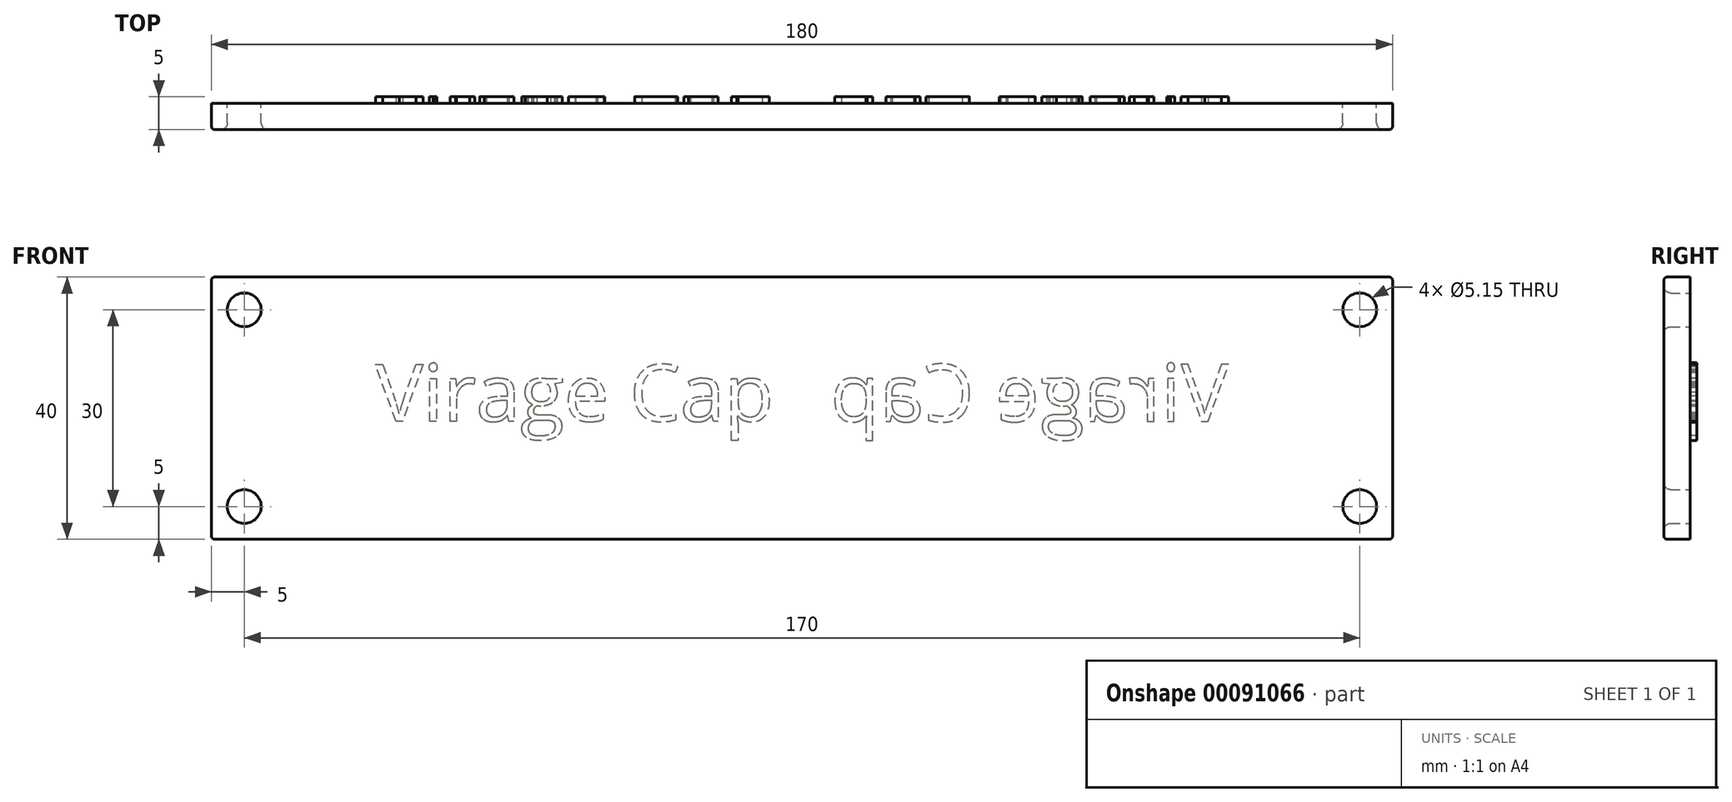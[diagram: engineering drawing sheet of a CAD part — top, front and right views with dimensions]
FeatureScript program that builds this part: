
annotation { "Feature Type Name" : "Feature", "Feature Type Description" : "" }
export const myFeature = defineFeature(function(context is Context, id is Id, definition is map)
    precondition{}
    {
        {
            var Q0;
            Q0=qCreatedBy(makeId("Front.planeOp"),FACE);
            var sketch = newSketch(context, id + "F0", { "sketchPlane" : qUnion([Q0])});
            skLineSegment(sketch, "E0.bottom", {"start": v(-90, -20) * mm, "end": v(90, -20) * mm});
            skLineSegment(sketch, "E0.top", {"start": v(-90, 20) * mm, "end": v(90, 20) * mm});
            skLineSegment(sketch, "E0.left", {"start": v(-90, -20) * mm, "end": v(-90, 20) * mm});
            skLineSegment(sketch, "E0.right", {"start": v(90, -20) * mm, "end": v(90, 20) * mm});
            skPoint(sketch, "E0.middle", {"position": v(0, 0) * mm});
            skCircle(sketch, "E1", {"center": v(-85, 15) * mm, "radius": 2.58 * mm});
            skPoint(sketch, "E2.start.orphan", {"position": v(-90, 0) * mm});
            skPoint(sketch, "E3.orphan", {"position": v(0, 20) * mm});
            skPoint(sketch, "E4.end.orphan", {"position": v(0, -20) * mm});
            skLineSegment(sketch, "E5", {"start": v(-90, 0) * mm, "end": v(0, 0) * mm, "construction": true});
            skLineSegment(sketch, "E6", {"start": v(0, 20) * mm, "end": v(0, -20) * mm, "construction": true});
            skCircle(sketch, "E7.MirrorC", {"center": v(-85, -15) * mm, "radius": 2.58 * mm});
            skCircle(sketch, "E8.MirrorC", {"center": v(85, 15) * mm, "radius": 2.58 * mm});
            skCircle(sketch, "E9.MirrorC", {"center": v(85, -15) * mm, "radius": 2.58 * mm});
            skSolve(sketch);
        }
        {
            var Q0;
            Q0=makeQuery(id+"F0.imprint","IMPRINT",FACE,{"disambiguationData":[TD([[makeQuery(id+"F0.imprint","IMPRINT",EDGE,{"derivedFrom":sQuery(id+"F0.wireOp",EDGE,"E0.bottom")}),1.0]])]});
            extrude(context, id + "F1", {"entities" : qUnion([Q0]), "depth" : 4 * mm});
        }
        {
            var Q0;
            Q0=makeQuery(id+"F1.opExtrude","CAP_EDGE",EDGE,{"disambiguationData":[OSD([sQuery(id+"F0.wireOp",EDGE,"E1")])],"isStart":false});
            var Q1;
            Q1=makeQuery(id+"F1.opExtrude","CAP_EDGE",EDGE,{"disambiguationData":[OSD([sQuery(id+"F0.wireOp",EDGE,"f5b72a5b-8583-449a-bdbf-9ac5a681e1fd0.MirrorC")])],"isStart":false});
            var Q2;
            Q2=makeQuery(id+"F1.opExtrude","CAP_EDGE",EDGE,{"disambiguationData":[OSD([sQuery(id+"F0.wireOp",EDGE,"2623e306-60f4-4522-aa65-1e3e8c2cf5b60.MirrorC")])],"isStart":false});
            var Q3;
            Q3=makeQuery(id+"F1.opExtrude","CAP_EDGE",EDGE,{"disambiguationData":[OSD([sQuery(id+"F0.wireOp",EDGE,"be81a34d-1d50-4ce7-a7a8-4484a1701fac0.MirrorC")])],"isStart":false});
            var Q4;
            Q4=makeQuery(id+"F1.opExtrude","CAP_EDGE",EDGE,{"disambiguationData":[OSD([sQuery(id+"F0.wireOp",EDGE,"E7.MirrorC")])],"isStart":false});
            var Q5;
            Q5=makeQuery(id+"F1.opExtrude","CAP_EDGE",EDGE,{"disambiguationData":[OSD([sQuery(id+"F0.wireOp",EDGE,"E8.MirrorC")])],"isStart":false});
            var Q6;
            Q6=makeQuery(id+"F1.opExtrude","CAP_EDGE",EDGE,{"disambiguationData":[OSD([sQuery(id+"F0.wireOp",EDGE,"E9.MirrorC")])],"isStart":false});
            fillet(context, id + "F2", {"entities" : qUnion([Q0, Q1, Q2, Q3, Q4, Q5, Q6]), "radius" : 1 * mm, "tangentPropagation" : true, "allowEdgeOverflow" : false});
        }
        {
            var Q0;
            Q0=makeQuery(id+"F1.opExtrude","CAP_EDGE",EDGE,{"disambiguationData":[OSD([sQuery(id+"F0.wireOp",EDGE,"E0.top")])],"isStart":false});
            var Q1;
            Q1=makeQuery(id+"F1.opExtrude","CAP_EDGE",EDGE,{"disambiguationData":[OSD([sQuery(id+"F0.wireOp",EDGE,"E0.left")])],"isStart":false});
            var Q2;
            Q2=makeQuery(id+"F1.opExtrude","CAP_EDGE",EDGE,{"disambiguationData":[OSD([sQuery(id+"F0.wireOp",EDGE,"E0.bottom")])],"isStart":false});
            var Q3;
            Q3=makeQuery(id+"F1.opExtrude","CAP_EDGE",EDGE,{"disambiguationData":[OSD([sQuery(id+"F0.wireOp",EDGE,"E0.right")])],"isStart":false});
            var Q4;
            Q4=makeQuery(id+"F1.opExtrude","SWEPT_EDGE",EDGE,{"disambiguationData":[OSD([sQuery(id+"F0.wireOp",EDGE,"E0.top"),sQuery(id+"F0.wireOp",EDGE,"E0.left")])]});
            var Q5;
            Q5=makeQuery(id+"F1.opExtrude","SWEPT_EDGE",EDGE,{"disambiguationData":[OSD([sQuery(id+"F0.wireOp",EDGE,"E0.bottom"),sQuery(id+"F0.wireOp",EDGE,"E0.left")])]});
            var Q6;
            Q6=makeQuery(id+"F1.opExtrude","SWEPT_EDGE",EDGE,{"disambiguationData":[OSD([sQuery(id+"F0.wireOp",EDGE,"E0.top"),sQuery(id+"F0.wireOp",EDGE,"E0.right")])]});
            var Q7;
            Q7=makeQuery(id+"F1.opExtrude","SWEPT_EDGE",EDGE,{"disambiguationData":[OSD([sQuery(id+"F0.wireOp",EDGE,"E0.bottom"),sQuery(id+"F0.wireOp",EDGE,"E0.right")])]});
            fillet(context, id + "F3", {"entities" : qUnion([Q0, Q1, Q2, Q3, Q4, Q5, Q6, Q7]), "radius" : .5 * mm, "tangentPropagation" : true, "allowEdgeOverflow" : false});
        }
        {
            var Q0;
            Q0=makeQuery(id+"F1.opExtrude","CAP_FACE",FACE,{"disambiguationData":[OSD([sQuery(id+"F0.wireOp",EDGE,"E0.bottom"),sQuery(id+"F0.wireOp",EDGE,"E0.top"),sQuery(id+"F0.wireOp",EDGE,"E0.left"),sQuery(id+"F0.wireOp",EDGE,"E0.right"),sQuery(id+"F0.wireOp",EDGE,"E1"),sQuery(id+"F0.wireOp",EDGE,"E7.MirrorC"),sQuery(id+"F0.wireOp",EDGE,"E8.MirrorC"),sQuery(id+"F0.wireOp",EDGE,"E9.MirrorC")])],"isStart":true});
            var sketch = newSketch(context, id + "F4", { "sketchPlane" : qUnion([Q0])});
            skText(sketch, "E10", { "text": "Virage Cap", "fontName": "OpenSans-Regular.ttf"});
            skLineSegment(sketch, "E11", {"start": v(0, 20) * mm, "end": v(0, -20) * mm, "construction": true});
            const initialGuessF4  = {"E10": [-0.065, -0.00202, 1, 0, 0.00877]};
            skSetInitialGuess(sketch, initialGuessF4);
            skSolve(sketch);
        }
        {
            var Q0;
            Q0 = qSketchRegion(id + "F4", true);
            extrude(context, id + "F5", {"entities" : qUnion([Q0]), "operationType" : NewBodyOperationType.ADD, "depth" : 1 * mm});
        }
        {
            var Q0;
            Q0=makeQuery(id+"F1.opExtrude","SWEPT_BODY",BODY,{"disambiguationData":[OSD([sQuery(id+"F0.wireOp",EDGE,"E0.bottom"),sQuery(id+"F0.wireOp",EDGE,"E0.top"),sQuery(id+"F0.wireOp",EDGE,"E0.left"),sQuery(id+"F0.wireOp",EDGE,"E0.right"),sQuery(id+"F0.wireOp",EDGE,"E1"),sQuery(id+"F0.wireOp",EDGE,"E7.MirrorC"),sQuery(id+"F0.wireOp",EDGE,"E8.MirrorC"),sQuery(id+"F0.wireOp",EDGE,"E9.MirrorC")])]});
            var Q1;
            Q1=makeQuery(id+"F5.opExtrude","SWEPT_FACE",FACE,{"disambiguationData":[OSD([sQuery(id+"F4.wireOp",EDGE,"E10.sketch_text.stroke-94")])]});
            var Q2;
            Q2=makeQuery(id+"F5.opExtrude","SWEPT_FACE",FACE,{"disambiguationData":[OSD([sQuery(id+"F4.wireOp",EDGE,"E10.sketch_text.stroke-169")])]});
            var Q3;
            Q3=makeQuery(id+"F5.opExtrude","SWEPT_FACE",FACE,{"disambiguationData":[OSD([sQuery(id+"F4.wireOp",EDGE,"E10.sketch_text.stroke-185")])]});
            var Q4;
            Q4=makeQuery(id+"F5.opExtrude","SWEPT_FACE",FACE,{"disambiguationData":[OSD([sQuery(id+"F4.wireOp",EDGE,"E10.sketch_text.stroke-125")])]});
            var Q5;
            Q5=makeQuery(id+"F5.opExtrude","SWEPT_FACE",FACE,{"disambiguationData":[OSD([sQuery(id+"F4.wireOp",EDGE,"E10.sketch_text.stroke-155")])]});
            var Q6;
            Q6=makeQuery(id+"F5.opExtrude","SWEPT_FACE",FACE,{"disambiguationData":[OSD([sQuery(id+"F4.wireOp",EDGE,"E10.sketch_text.stroke-65")])]});
            var Q7;
            Q7=makeQuery(id+"F5.opExtrude","SWEPT_FACE",FACE,{"disambiguationData":[OSD([sQuery(id+"F4.wireOp",EDGE,"E10.sketch_text.stroke-81")])]});
            var Q8;
            Q8=makeQuery(id+"F5.opExtrude","SWEPT_FACE",FACE,{"disambiguationData":[OSD([sQuery(id+"F4.wireOp",EDGE,"E10.sketch_text.stroke-67")])]});
            var Q9;
            Q9=makeQuery(id+"F5.opExtrude","SWEPT_FACE",FACE,{"disambiguationData":[OSD([sQuery(id+"F4.wireOp",EDGE,"E10.sketch_text.stroke-99")])]});
            var Q10;
            Q10=makeQuery(id+"F5.opExtrude","SWEPT_FACE",FACE,{"disambiguationData":[OSD([sQuery(id+"F4.wireOp",EDGE,"E10.sketch_text.stroke-127")])]});
            var Q11;
            Q11=makeQuery(id+"F5.opExtrude","SWEPT_FACE",FACE,{"disambiguationData":[OSD([sQuery(id+"F4.wireOp",EDGE,"E10.sketch_text.stroke-10")])]});
            var Q12;
            Q12=makeQuery(id+"F5.opExtrude","CAP_FACE",FACE,{"disambiguationData":[OSD([sQuery(id+"F4.wireOp",EDGE,"E10.sketch_text.stroke-9"),sQuery(id+"F4.wireOp",EDGE,"E10.sketch_text.stroke-10"),sQuery(id+"F4.wireOp",EDGE,"E10.sketch_text.stroke-11"),sQuery(id+"F4.wireOp",EDGE,"E10.sketch_text.stroke-12")])],"isStart":false});
            var Q13;
            Q13=makeQuery(id+"F5.opExtrude","SWEPT_FACE",FACE,{"disambiguationData":[OSD([sQuery(id+"F4.wireOp",EDGE,"E10.sketch_text.stroke-154")])]});
            var Q14;
            Q14=makeQuery(id+"F5.opExtrude","SWEPT_FACE",FACE,{"disambiguationData":[OSD([sQuery(id+"F4.wireOp",EDGE,"E10.sketch_text.stroke-1")])]});
            var Q15;
            Q15=makeQuery(id+"F5.opExtrude","CAP_FACE",FACE,{"disambiguationData":[OSD([sQuery(id+"F4.wireOp",EDGE,"E10.sketch_text.stroke-124"),sQuery(id+"F4.wireOp",EDGE,"E10.sketch_text.stroke-125"),sQuery(id+"F4.wireOp",EDGE,"E10.sketch_text.stroke-126"),sQuery(id+"F4.wireOp",EDGE,"E10.sketch_text.stroke-127"),sQuery(id+"F4.wireOp",EDGE,"E10.sketch_text.stroke-128"),sQuery(id+"F4.wireOp",EDGE,"E10.sketch_text.stroke-129"),sQuery(id+"F4.wireOp",EDGE,"E10.sketch_text.stroke-130"),sQuery(id+"F4.wireOp",EDGE,"E10.sketch_text.stroke-131"),sQuery(id+"F4.wireOp",EDGE,"E10.sketch_text.stroke-132"),sQuery(id+"F4.wireOp",EDGE,"E10.sketch_text.stroke-133"),sQuery(id+"F4.wireOp",EDGE,"E10.sketch_text.stroke-134"),sQuery(id+"F4.wireOp",EDGE,"E10.sketch_text.stroke-135"),sQuery(id+"F4.wireOp",EDGE,"E10.sketch_text.stroke-136"),sQuery(id+"F4.wireOp",EDGE,"E10.sketch_text.stroke-137"),sQuery(id+"F4.wireOp",EDGE,"E10.sketch_text.stroke-138")])],"isStart":false});
            var Q16;
            Q16=makeQuery(id+"F5.opExtrude","CAP_FACE",FACE,{"disambiguationData":[OSD([sQuery(id+"F4.wireOp",EDGE,"E10.sketch_text.stroke-34"),sQuery(id+"F4.wireOp",EDGE,"E10.sketch_text.stroke-35"),sQuery(id+"F4.wireOp",EDGE,"E10.sketch_text.stroke-36"),sQuery(id+"F4.wireOp",EDGE,"E10.sketch_text.stroke-37"),sQuery(id+"F4.wireOp",EDGE,"E10.sketch_text.stroke-38"),sQuery(id+"F4.wireOp",EDGE,"E10.sketch_text.stroke-39"),sQuery(id+"F4.wireOp",EDGE,"E10.sketch_text.stroke-40"),sQuery(id+"F4.wireOp",EDGE,"E10.sketch_text.stroke-41"),sQuery(id+"F4.wireOp",EDGE,"E10.sketch_text.stroke-42"),sQuery(id+"F4.wireOp",EDGE,"E10.sketch_text.stroke-43"),sQuery(id+"F4.wireOp",EDGE,"E10.sketch_text.stroke-44"),sQuery(id+"F4.wireOp",EDGE,"E10.sketch_text.stroke-45"),sQuery(id+"F4.wireOp",EDGE,"E10.sketch_text.stroke-46"),sQuery(id+"F4.wireOp",EDGE,"E10.sketch_text.stroke-47"),sQuery(id+"F4.wireOp",EDGE,"E10.sketch_text.stroke-48"),sQuery(id+"F4.wireOp",EDGE,"E10.sketch_text.stroke-49"),sQuery(id+"F4.wireOp",EDGE,"E10.sketch_text.stroke-50"),sQuery(id+"F4.wireOp",EDGE,"E10.sketch_text.stroke-51"),sQuery(id+"F4.wireOp",EDGE,"E10.sketch_text.stroke-52"),sQuery(id+"F4.wireOp",EDGE,"E10.sketch_text.stroke-53"),sQuery(id+"F4.wireOp",EDGE,"E10.sketch_text.stroke-54"),sQuery(id+"F4.wireOp",EDGE,"E10.sketch_text.stroke-55"),sQuery(id+"F4.wireOp",EDGE,"E10.sketch_text.stroke-56"),sQuery(id+"F4.wireOp",EDGE,"E10.sketch_text.stroke-57"),sQuery(id+"F4.wireOp",EDGE,"E10.sketch_text.stroke-58"),sQuery(id+"F4.wireOp",EDGE,"E10.sketch_text.stroke-59"),sQuery(id+"F4.wireOp",EDGE,"E10.sketch_text.stroke-60")])],"isStart":false});
            var Q17;
            Q17=makeQuery(id+"F5.opExtrude","SWEPT_FACE",FACE,{"disambiguationData":[OSD([sQuery(id+"F4.wireOp",EDGE,"E10.sketch_text.stroke-50")])]});
            var Q18;
            Q18=makeQuery(id+"F5.opExtrude","SWEPT_FACE",FACE,{"disambiguationData":[OSD([sQuery(id+"F4.wireOp",EDGE,"E10.sketch_text.stroke-2")])]});
            var Q19;
            Q19=makeQuery(id+"F5.opExtrude","SWEPT_FACE",FACE,{"disambiguationData":[OSD([sQuery(id+"F4.wireOp",EDGE,"E10.sketch_text.stroke-3")])]});
            var Q20;
            Q20=makeQuery(id+"F5.opExtrude","SWEPT_FACE",FACE,{"disambiguationData":[OSD([sQuery(id+"F4.wireOp",EDGE,"E10.sketch_text.stroke-5")])]});
            var Q21;
            Q21=makeQuery(id+"F5.opExtrude","SWEPT_FACE",FACE,{"disambiguationData":[OSD([sQuery(id+"F4.wireOp",EDGE,"E10.sketch_text.stroke-8")])]});
            var Q22;
            Q22=makeQuery(id+"F5.opExtrude","SWEPT_FACE",FACE,{"disambiguationData":[OSD([sQuery(id+"F4.wireOp",EDGE,"E10.sketch_text.stroke-98")])]});
            var Q23;
            Q23=makeQuery(id+"F5.opExtrude","SWEPT_FACE",FACE,{"disambiguationData":[OSD([sQuery(id+"F4.wireOp",EDGE,"E10.sketch_text.stroke-66")])]});
            var Q24;
            Q24=makeQuery(id+"F5.opExtrude","SWEPT_FACE",FACE,{"disambiguationData":[OSD([sQuery(id+"F4.wireOp",EDGE,"E10.sketch_text.stroke-153")])]});
            var Q25;
            Q25=makeQuery(id+"F5.opExtrude","SWEPT_FACE",FACE,{"disambiguationData":[OSD([sQuery(id+"F4.wireOp",EDGE,"E10.sketch_text.stroke-126")])]});
            var Q26;
            Q26=makeQuery(id+"F5.opExtrude","SWEPT_FACE",FACE,{"disambiguationData":[OSD([sQuery(id+"F4.wireOp",EDGE,"E10.sketch_text.stroke-183")])]});
            var Q27;
            Q27=makeQuery(id+"F5.opExtrude","SWEPT_FACE",FACE,{"disambiguationData":[OSD([sQuery(id+"F4.wireOp",EDGE,"E10.sketch_text.stroke-109")])]});
            var Q28;
            Q28=makeQuery(id+"F5.opExtrude","SWEPT_FACE",FACE,{"disambiguationData":[OSD([sQuery(id+"F4.wireOp",EDGE,"E10.sketch_text.stroke-186")])]});
            var Q29;
            Q29=makeQuery(id+"F5.opExtrude","SWEPT_FACE",FACE,{"disambiguationData":[OSD([sQuery(id+"F4.wireOp",EDGE,"E10.sketch_text.stroke-79")])]});
            var Q30;
            Q30=makeQuery(id+"F5.opExtrude","SWEPT_FACE",FACE,{"disambiguationData":[OSD([sQuery(id+"F4.wireOp",EDGE,"E10.sketch_text.stroke-110")])]});
            var Q31;
            Q31=makeQuery(id+"F5.opExtrude","SWEPT_FACE",FACE,{"disambiguationData":[OSD([sQuery(id+"F4.wireOp",EDGE,"E10.sketch_text.stroke-38")])]});
            var Q32;
            Q32=makeQuery(id+"F5.opExtrude","SWEPT_FACE",FACE,{"disambiguationData":[OSD([sQuery(id+"F4.wireOp",EDGE,"E10.sketch_text.stroke-24")])]});
            var Q33;
            Q33=makeQuery(id+"F5.opExtrude","SWEPT_FACE",FACE,{"disambiguationData":[OSD([sQuery(id+"F4.wireOp",EDGE,"E10.sketch_text.stroke-12")])]});
            var Q34;
            Q34=makeQuery(id+"F5.opExtrude","SWEPT_FACE",FACE,{"disambiguationData":[OSD([sQuery(id+"F4.wireOp",EDGE,"E10.sketch_text.stroke-100")])]});
            var Q35;
            Q35=makeQuery(id+"F5.opExtrude","SWEPT_FACE",FACE,{"disambiguationData":[OSD([sQuery(id+"F4.wireOp",EDGE,"E10.sketch_text.stroke-158")])]});
            var Q36;
            Q36=makeQuery(id+"F5.opExtrude","SWEPT_FACE",FACE,{"disambiguationData":[OSD([sQuery(id+"F4.wireOp",EDGE,"E10.sketch_text.stroke-142")])]});
            var Q37;
            Q37=makeQuery(id+"F5.opExtrude","SWEPT_FACE",FACE,{"disambiguationData":[OSD([sQuery(id+"F4.wireOp",EDGE,"E10.sketch_text.stroke-54")])]});
            var Q38;
            Q38=makeQuery(id+"F5.opExtrude","SWEPT_FACE",FACE,{"disambiguationData":[OSD([sQuery(id+"F4.wireOp",EDGE,"E10.sketch_text.stroke-25")])]});
            var Q39;
            Q39=makeQuery(id+"F5.opExtrude","SWEPT_FACE",FACE,{"disambiguationData":[OSD([sQuery(id+"F4.wireOp",EDGE,"E10.sketch_text.stroke-101")])]});
            var Q40;
            Q40=makeQuery(id+"F5.opExtrude","SWEPT_FACE",FACE,{"disambiguationData":[OSD([sQuery(id+"F4.wireOp",EDGE,"E10.sketch_text.stroke-69")])]});
            var Q41;
            Q41=makeQuery(id+"F5.opExtrude","SWEPT_FACE",FACE,{"disambiguationData":[OSD([sQuery(id+"F4.wireOp",EDGE,"E10.sketch_text.stroke-159")])]});
            var Q42;
            Q42=makeQuery(id+"F5.opExtrude","SWEPT_FACE",FACE,{"disambiguationData":[OSD([sQuery(id+"F4.wireOp",EDGE,"E10.sketch_text.stroke-85")])]});
            var Q43;
            Q43=makeQuery(id+"F5.opExtrude","SWEPT_FACE",FACE,{"disambiguationData":[OSD([sQuery(id+"F4.wireOp",EDGE,"E10.sketch_text.stroke-173")])]});
            var Q44;
            Q44=makeQuery(id+"F5.opExtrude","SWEPT_FACE",FACE,{"disambiguationData":[OSD([sQuery(id+"F4.wireOp",EDGE,"E10.sketch_text.stroke-40")])]});
            var Q45;
            Q45=makeQuery(id+"F5.opExtrude","SWEPT_FACE",FACE,{"disambiguationData":[OSD([sQuery(id+"F4.wireOp",EDGE,"E10.sketch_text.stroke-102")])]});
            var Q46;
            Q46=makeQuery(id+"F5.opExtrude","SWEPT_FACE",FACE,{"disambiguationData":[OSD([sQuery(id+"F4.wireOp",EDGE,"E10.sketch_text.stroke-86")])]});
            var Q47;
            Q47=makeQuery(id+"F5.opExtrude","SWEPT_FACE",FACE,{"disambiguationData":[OSD([sQuery(id+"F4.wireOp",EDGE,"E10.sketch_text.stroke-130")])]});
            var Q48;
            Q48=makeQuery(id+"F5.opExtrude","SWEPT_FACE",FACE,{"disambiguationData":[OSD([sQuery(id+"F4.wireOp",EDGE,"E10.sketch_text.stroke-103")])]});
            var Q49;
            Q49=makeQuery(id+"F5.opExtrude","SWEPT_FACE",FACE,{"disambiguationData":[OSD([sQuery(id+"F4.wireOp",EDGE,"E10.sketch_text.stroke-87")])]});
            var Q50;
            Q50=makeQuery(id+"F5.opExtrude","SWEPT_FACE",FACE,{"disambiguationData":[OSD([sQuery(id+"F4.wireOp",EDGE,"E10.sketch_text.stroke-145")])]});
            var Q51;
            Q51=makeQuery(id+"F5.opExtrude","SWEPT_FACE",FACE,{"disambiguationData":[OSD([sQuery(id+"F4.wireOp",EDGE,"E10.sketch_text.stroke-131")])]});
            var Q52;
            Q52=makeQuery(id+"F5.opExtrude","SWEPT_FACE",FACE,{"disambiguationData":[OSD([sQuery(id+"F4.wireOp",EDGE,"E10.sketch_text.stroke-28")])]});
            var Q53;
            Q53=makeQuery(id+"F5.opExtrude","SWEPT_FACE",FACE,{"disambiguationData":[OSD([sQuery(id+"F4.wireOp",EDGE,"E10.sketch_text.stroke-14")])]});
            var Q54;
            Q54=makeQuery(id+"F5.opExtrude","SWEPT_FACE",FACE,{"disambiguationData":[OSD([sQuery(id+"F4.wireOp",EDGE,"E10.sketch_text.stroke-88")])]});
            var Q55;
            Q55=makeQuery(id+"F5.opExtrude","SWEPT_FACE",FACE,{"disambiguationData":[OSD([sQuery(id+"F4.wireOp",EDGE,"E10.sketch_text.stroke-162")])]});
            var Q56;
            Q56=makeQuery(id+"F5.opExtrude","SWEPT_FACE",FACE,{"disambiguationData":[OSD([sQuery(id+"F4.wireOp",EDGE,"E10.sketch_text.stroke-176")])]});
            var Q57;
            Q57=makeQuery(id+"F5.opExtrude","SWEPT_FACE",FACE,{"disambiguationData":[OSD([sQuery(id+"F4.wireOp",EDGE,"E10.sketch_text.stroke-73")])]});
            var Q58;
            Q58=makeQuery(id+"F5.opExtrude","SWEPT_FACE",FACE,{"disambiguationData":[OSD([sQuery(id+"F4.wireOp",EDGE,"E10.sketch_text.stroke-59")])]});
            var Q59;
            Q59=makeQuery(id+"F5.opExtrude","SWEPT_FACE",FACE,{"disambiguationData":[OSD([sQuery(id+"F4.wireOp",EDGE,"E10.sketch_text.stroke-133")])]});
            var Q60;
            Q60=makeQuery(id+"F5.opExtrude","SWEPT_FACE",FACE,{"disambiguationData":[OSD([sQuery(id+"F4.wireOp",EDGE,"E10.sketch_text.stroke-119")])]});
            var Q61;
            Q61=makeQuery(id+"F5.opExtrude","SWEPT_FACE",FACE,{"disambiguationData":[OSD([sQuery(id+"F4.wireOp",EDGE,"E10.sketch_text.stroke-74")])]});
            var Q62;
            Q62=makeQuery(id+"F5.opExtrude","SWEPT_FACE",FACE,{"disambiguationData":[OSD([sQuery(id+"F4.wireOp",EDGE,"E10.sketch_text.stroke-44")])]});
            var Q63;
            Q63=makeQuery(id+"F5.opExtrude","SWEPT_FACE",FACE,{"disambiguationData":[OSD([sQuery(id+"F4.wireOp",EDGE,"E10.sketch_text.stroke-120")])]});
            var Q64;
            Q64=makeQuery(id+"F5.opExtrude","SWEPT_FACE",FACE,{"disambiguationData":[OSD([sQuery(id+"F4.wireOp",EDGE,"E10.sketch_text.stroke-90")])]});
            var Q65;
            Q65=makeQuery(id+"F5.opExtrude","SWEPT_FACE",FACE,{"disambiguationData":[OSD([sQuery(id+"F4.wireOp",EDGE,"E10.sketch_text.stroke-178")])]});
            var Q66;
            Q66=makeQuery(id+"F5.opExtrude","SWEPT_FACE",FACE,{"disambiguationData":[OSD([sQuery(id+"F4.wireOp",EDGE,"E10.sketch_text.stroke-45")])]});
            var Q67;
            Q67=makeQuery(id+"F5.opExtrude","SWEPT_FACE",FACE,{"disambiguationData":[OSD([sQuery(id+"F4.wireOp",EDGE,"E10.sketch_text.stroke-31")])]});
            var Q68;
            Q68=makeQuery(id+"F5.opExtrude","SWEPT_FACE",FACE,{"disambiguationData":[OSD([sQuery(id+"F4.wireOp",EDGE,"E10.sketch_text.stroke-135")])]});
            var Q69;
            Q69=makeQuery(id+"F5.opExtrude","SWEPT_FACE",FACE,{"disambiguationData":[OSD([sQuery(id+"F4.wireOp",EDGE,"E10.sketch_text.stroke-179")])]});
            var Q70;
            Q70=makeQuery(id+"F5.opExtrude","SWEPT_FACE",FACE,{"disambiguationData":[OSD([sQuery(id+"F4.wireOp",EDGE,"E10.sketch_text.stroke-165")])]});
            var Q71;
            Q71=makeQuery(id+"F5.opExtrude","SWEPT_FACE",FACE,{"disambiguationData":[OSD([sQuery(id+"F4.wireOp",EDGE,"E10.sketch_text.stroke-149")])]});
            var Q72;
            Q72=makeQuery(id+"F5.opExtrude","SWEPT_FACE",FACE,{"disambiguationData":[OSD([sQuery(id+"F4.wireOp",EDGE,"E10.sketch_text.stroke-136")])]});
            var Q73;
            Q73=makeQuery(id+"F5.opExtrude","SWEPT_FACE",FACE,{"disambiguationData":[OSD([sQuery(id+"F4.wireOp",EDGE,"E10.sketch_text.stroke-122")])]});
            var Q74;
            Q74=makeQuery(id+"F5.opExtrude","SWEPT_FACE",FACE,{"disambiguationData":[OSD([sQuery(id+"F4.wireOp",EDGE,"E10.sketch_text.stroke-106")])]});
            var Q75;
            Q75=makeQuery(id+"F5.opExtrude","SWEPT_FACE",FACE,{"disambiguationData":[OSD([sQuery(id+"F4.wireOp",EDGE,"E10.sketch_text.stroke-180")])]});
            var Q76;
            Q76=makeQuery(id+"F5.opExtrude","SWEPT_FACE",FACE,{"disambiguationData":[OSD([sQuery(id+"F4.wireOp",EDGE,"E10.sketch_text.stroke-166")])]});
            var Q77;
            Q77=makeQuery(id+"F5.opExtrude","SWEPT_FACE",FACE,{"disambiguationData":[OSD([sQuery(id+"F4.wireOp",EDGE,"E10.sketch_text.stroke-150")])]});
            var Q78;
            Q78=makeQuery(id+"F5.opExtrude","SWEPT_FACE",FACE,{"disambiguationData":[OSD([sQuery(id+"F4.wireOp",EDGE,"E10.sketch_text.stroke-76")])]});
            var Q79;
            Q79=makeQuery(id+"F5.opExtrude","SWEPT_FACE",FACE,{"disambiguationData":[OSD([sQuery(id+"F4.wireOp",EDGE,"E10.sketch_text.stroke-32")])]});
            var Q80;
            Q80=makeQuery(id+"F5.opExtrude","SWEPT_FACE",FACE,{"disambiguationData":[OSD([sQuery(id+"F4.wireOp",EDGE,"E10.sketch_text.stroke-181")])]});
            var Q81;
            Q81=makeQuery(id+"F5.opExtrude","SWEPT_FACE",FACE,{"disambiguationData":[OSD([sQuery(id+"F4.wireOp",EDGE,"E10.sketch_text.stroke-47")])]});
            var Q82;
            Q82=makeQuery(id+"F5.opExtrude","SWEPT_FACE",FACE,{"disambiguationData":[OSD([sQuery(id+"F4.wireOp",EDGE,"E10.sketch_text.stroke-123")])]});
            var Q83;
            Q83=makeQuery(id+"F5.opExtrude","SWEPT_FACE",FACE,{"disambiguationData":[OSD([sQuery(id+"F4.wireOp",EDGE,"E10.sketch_text.stroke-107")])]});
            var Q84;
            Q84=makeQuery(id+"F5.opExtrude","SWEPT_FACE",FACE,{"disambiguationData":[OSD([sQuery(id+"F4.wireOp",EDGE,"E10.sketch_text.stroke-48")])]});
            var Q85;
            Q85=makeQuery(id+"F5.opExtrude","SWEPT_FACE",FACE,{"disambiguationData":[OSD([sQuery(id+"F4.wireOp",EDGE,"E10.sketch_text.stroke-124")])]});
            var Q86;
            Q86=makeQuery(id+"F5.opExtrude","SWEPT_FACE",FACE,{"disambiguationData":[OSD([sQuery(id+"F4.wireOp",EDGE,"E10.sketch_text.stroke-108")])]});
            var Q87;
            Q87=makeQuery(id+"F5.opExtrude","CAP_FACE",FACE,{"disambiguationData":[OSD([sQuery(id+"F4.wireOp",EDGE,"E10.sketch_text.stroke-139"),sQuery(id+"F4.wireOp",EDGE,"E10.sketch_text.stroke-140"),sQuery(id+"F4.wireOp",EDGE,"E10.sketch_text.stroke-141"),sQuery(id+"F4.wireOp",EDGE,"E10.sketch_text.stroke-142"),sQuery(id+"F4.wireOp",EDGE,"E10.sketch_text.stroke-143"),sQuery(id+"F4.wireOp",EDGE,"E10.sketch_text.stroke-144"),sQuery(id+"F4.wireOp",EDGE,"E10.sketch_text.stroke-145"),sQuery(id+"F4.wireOp",EDGE,"E10.sketch_text.stroke-146"),sQuery(id+"F4.wireOp",EDGE,"E10.sketch_text.stroke-147"),sQuery(id+"F4.wireOp",EDGE,"E10.sketch_text.stroke-148"),sQuery(id+"F4.wireOp",EDGE,"E10.sketch_text.stroke-149"),sQuery(id+"F4.wireOp",EDGE,"E10.sketch_text.stroke-150"),sQuery(id+"F4.wireOp",EDGE,"E10.sketch_text.stroke-151"),sQuery(id+"F4.wireOp",EDGE,"E10.sketch_text.stroke-152"),sQuery(id+"F4.wireOp",EDGE,"E10.sketch_text.stroke-153"),sQuery(id+"F4.wireOp",EDGE,"E10.sketch_text.stroke-154"),sQuery(id+"F4.wireOp",EDGE,"E10.sketch_text.stroke-155"),sQuery(id+"F4.wireOp",EDGE,"E10.sketch_text.stroke-156"),sQuery(id+"F4.wireOp",EDGE,"E10.sketch_text.stroke-157"),sQuery(id+"F4.wireOp",EDGE,"E10.sketch_text.stroke-158"),sQuery(id+"F4.wireOp",EDGE,"E10.sketch_text.stroke-159"),sQuery(id+"F4.wireOp",EDGE,"E10.sketch_text.stroke-160"),sQuery(id+"F4.wireOp",EDGE,"E10.sketch_text.stroke-161"),sQuery(id+"F4.wireOp",EDGE,"E10.sketch_text.stroke-162"),sQuery(id+"F4.wireOp",EDGE,"E10.sketch_text.stroke-163"),sQuery(id+"F4.wireOp",EDGE,"E10.sketch_text.stroke-164"),sQuery(id+"F4.wireOp",EDGE,"E10.sketch_text.stroke-165")])],"isStart":false});
            var Q88;
            Q88=makeQuery(id+"F5.opExtrude","CAP_FACE",FACE,{"disambiguationData":[OSD([sQuery(id+"F4.wireOp",EDGE,"E10.sketch_text.stroke-21"),sQuery(id+"F4.wireOp",EDGE,"E10.sketch_text.stroke-22"),sQuery(id+"F4.wireOp",EDGE,"E10.sketch_text.stroke-23"),sQuery(id+"F4.wireOp",EDGE,"E10.sketch_text.stroke-24"),sQuery(id+"F4.wireOp",EDGE,"E10.sketch_text.stroke-25"),sQuery(id+"F4.wireOp",EDGE,"E10.sketch_text.stroke-26"),sQuery(id+"F4.wireOp",EDGE,"E10.sketch_text.stroke-27"),sQuery(id+"F4.wireOp",EDGE,"E10.sketch_text.stroke-28"),sQuery(id+"F4.wireOp",EDGE,"E10.sketch_text.stroke-29"),sQuery(id+"F4.wireOp",EDGE,"E10.sketch_text.stroke-30"),sQuery(id+"F4.wireOp",EDGE,"E10.sketch_text.stroke-31"),sQuery(id+"F4.wireOp",EDGE,"E10.sketch_text.stroke-32"),sQuery(id+"F4.wireOp",EDGE,"E10.sketch_text.stroke-33")])],"isStart":false});
            var Q89;
            Q89=makeQuery(id+"F5.opExtrude","SWEPT_FACE",FACE,{"disambiguationData":[OSD([sQuery(id+"F4.wireOp",EDGE,"E10.sketch_text.stroke-113")])]});
            var Q90;
            Q90=makeQuery(id+"F5.opExtrude","SWEPT_FACE",FACE,{"disambiguationData":[OSD([sQuery(id+"F4.wireOp",EDGE,"E10.sketch_text.stroke-37")])]});
            var Q91;
            Q91=makeQuery(id+"F5.opExtrude","SWEPT_FACE",FACE,{"disambiguationData":[OSD([sQuery(id+"F4.wireOp",EDGE,"E10.sketch_text.stroke-187")])]});
            var Q92;
            Q92=makeQuery(id+"F5.opExtrude","SWEPT_FACE",FACE,{"disambiguationData":[OSD([sQuery(id+"F4.wireOp",EDGE,"E10.sketch_text.stroke-0")])]});
            var Q93;
            Q93=makeQuery(id+"F5.opExtrude","SWEPT_FACE",FACE,{"disambiguationData":[OSD([sQuery(id+"F4.wireOp",EDGE,"E10.sketch_text.stroke-4")])]});
            var Q94;
            Q94=makeQuery(id+"F5.opExtrude","SWEPT_FACE",FACE,{"disambiguationData":[OSD([sQuery(id+"F4.wireOp",EDGE,"E10.sketch_text.stroke-82")])]});
            var Q95;
            Q95=makeQuery(id+"F5.opExtrude","SWEPT_FACE",FACE,{"disambiguationData":[OSD([sQuery(id+"F4.wireOp",EDGE,"E10.sketch_text.stroke-52")])]});
            var Q96;
            Q96=makeQuery(id+"F5.opExtrude","SWEPT_FACE",FACE,{"disambiguationData":[OSD([sQuery(id+"F4.wireOp",EDGE,"E10.sketch_text.stroke-49")])]});
            var Q97;
            Q97=makeQuery(id+"F5.opExtrude","SWEPT_FACE",FACE,{"disambiguationData":[OSD([sQuery(id+"F4.wireOp",EDGE,"E10.sketch_text.stroke-63")])]});
            var Q98;
            Q98=makeQuery(id+"F5.opExtrude","SWEPT_FACE",FACE,{"disambiguationData":[OSD([sQuery(id+"F4.wireOp",EDGE,"E10.sketch_text.stroke-21")])]});
            var Q99;
            Q99=makeQuery(id+"F5.opExtrude","SWEPT_FACE",FACE,{"disambiguationData":[OSD([sQuery(id+"F4.wireOp",EDGE,"E10.sketch_text.stroke-128")])]});
            var Q100;
            Q100=makeQuery(id+"F5.opExtrude","SWEPT_FACE",FACE,{"disambiguationData":[OSD([sQuery(id+"F4.wireOp",EDGE,"E10.sketch_text.stroke-55")])]});
            var Q101;
            Q101=makeQuery(id+"F5.opExtrude","SWEPT_FACE",FACE,{"disambiguationData":[OSD([sQuery(id+"F4.wireOp",EDGE,"E10.sketch_text.stroke-26")])]});
            var Q102;
            Q102=makeQuery(id+"F5.opExtrude","SWEPT_FACE",FACE,{"disambiguationData":[OSD([sQuery(id+"F4.wireOp",EDGE,"E10.sketch_text.stroke-174")])]});
            var Q103;
            Q103=makeQuery(id+"F5.opExtrude","SWEPT_FACE",FACE,{"disambiguationData":[OSD([sQuery(id+"F4.wireOp",EDGE,"E10.sketch_text.stroke-104")])]});
            var Q104;
            Q104=makeQuery(id+"F5.opExtrude","SWEPT_FACE",FACE,{"disambiguationData":[OSD([sQuery(id+"F4.wireOp",EDGE,"E10.sketch_text.stroke-72")])]});
            var Q105;
            Q105=makeQuery(id+"F5.opExtrude","SWEPT_FACE",FACE,{"disambiguationData":[OSD([sQuery(id+"F4.wireOp",EDGE,"E10.sketch_text.stroke-132")])]});
            var Q106;
            Q106=makeQuery(id+"F5.opExtrude","SWEPT_FACE",FACE,{"disambiguationData":[OSD([sQuery(id+"F4.wireOp",EDGE,"E10.sketch_text.stroke-43")])]});
            var Q107;
            Q107=makeQuery(id+"F5.opExtrude","SWEPT_FACE",FACE,{"disambiguationData":[OSD([sQuery(id+"F4.wireOp",EDGE,"E10.sketch_text.stroke-15")])]});
            var Q108;
            Q108=makeQuery(id+"F5.opExtrude","SWEPT_FACE",FACE,{"disambiguationData":[OSD([sQuery(id+"F4.wireOp",EDGE,"E10.sketch_text.stroke-89")])]});
            var Q109;
            Q109=makeQuery(id+"F5.opExtrude","SWEPT_FACE",FACE,{"disambiguationData":[OSD([sQuery(id+"F4.wireOp",EDGE,"E10.sketch_text.stroke-163")])]});
            var Q110;
            Q110=makeQuery(id+"F5.opExtrude","SWEPT_FACE",FACE,{"disambiguationData":[OSD([sQuery(id+"F4.wireOp",EDGE,"E10.sketch_text.stroke-30")])]});
            var Q111;
            Q111=makeQuery(id+"F5.opExtrude","SWEPT_FACE",FACE,{"disambiguationData":[OSD([sQuery(id+"F4.wireOp",EDGE,"E10.sketch_text.stroke-134")])]});
            var Q112;
            Q112=makeQuery(id+"F5.opExtrude","SWEPT_FACE",FACE,{"disambiguationData":[OSD([sQuery(id+"F4.wireOp",EDGE,"E10.sketch_text.stroke-121")])]});
            var Q113;
            Q113=makeQuery(id+"F5.opExtrude","CAP_FACE",FACE,{"disambiguationData":[OSD([sQuery(id+"F4.wireOp",EDGE,"E10.sketch_text.stroke-105"),sQuery(id+"F4.wireOp",EDGE,"E10.sketch_text.stroke-106"),sQuery(id+"F4.wireOp",EDGE,"E10.sketch_text.stroke-107"),sQuery(id+"F4.wireOp",EDGE,"E10.sketch_text.stroke-108"),sQuery(id+"F4.wireOp",EDGE,"E10.sketch_text.stroke-109"),sQuery(id+"F4.wireOp",EDGE,"E10.sketch_text.stroke-110"),sQuery(id+"F4.wireOp",EDGE,"E10.sketch_text.stroke-111"),sQuery(id+"F4.wireOp",EDGE,"E10.sketch_text.stroke-112"),sQuery(id+"F4.wireOp",EDGE,"E10.sketch_text.stroke-113"),sQuery(id+"F4.wireOp",EDGE,"E10.sketch_text.stroke-114"),sQuery(id+"F4.wireOp",EDGE,"E10.sketch_text.stroke-115"),sQuery(id+"F4.wireOp",EDGE,"E10.sketch_text.stroke-116"),sQuery(id+"F4.wireOp",EDGE,"E10.sketch_text.stroke-117"),sQuery(id+"F4.wireOp",EDGE,"E10.sketch_text.stroke-118"),sQuery(id+"F4.wireOp",EDGE,"E10.sketch_text.stroke-119"),sQuery(id+"F4.wireOp",EDGE,"E10.sketch_text.stroke-120"),sQuery(id+"F4.wireOp",EDGE,"E10.sketch_text.stroke-121"),sQuery(id+"F4.wireOp",EDGE,"E10.sketch_text.stroke-122"),sQuery(id+"F4.wireOp",EDGE,"E10.sketch_text.stroke-123")])],"isStart":false});
            var Q114;
            Q114=makeQuery(id+"F5.opExtrude","SWEPT_FACE",FACE,{"disambiguationData":[OSD([sQuery(id+"F4.wireOp",EDGE,"E10.sketch_text.stroke-92")])]});
            var Q115;
            Q115=makeQuery(id+"F5.opExtrude","SWEPT_FACE",FACE,{"disambiguationData":[OSD([sQuery(id+"F4.wireOp",EDGE,"E10.sketch_text.stroke-46")])]});
            var Q116;
            Q116=makeQuery(id+"F5.opExtrude","CAP_FACE",FACE,{"disambiguationData":[OSD([sQuery(id+"F4.wireOp",EDGE,"E10.sketch_text.stroke-61"),sQuery(id+"F4.wireOp",EDGE,"E10.sketch_text.stroke-62"),sQuery(id+"F4.wireOp",EDGE,"E10.sketch_text.stroke-63"),sQuery(id+"F4.wireOp",EDGE,"E10.sketch_text.stroke-64"),sQuery(id+"F4.wireOp",EDGE,"E10.sketch_text.stroke-65"),sQuery(id+"F4.wireOp",EDGE,"E10.sketch_text.stroke-66"),sQuery(id+"F4.wireOp",EDGE,"E10.sketch_text.stroke-67"),sQuery(id+"F4.wireOp",EDGE,"E10.sketch_text.stroke-68"),sQuery(id+"F4.wireOp",EDGE,"E10.sketch_text.stroke-69"),sQuery(id+"F4.wireOp",EDGE,"E10.sketch_text.stroke-70"),sQuery(id+"F4.wireOp",EDGE,"E10.sketch_text.stroke-71"),sQuery(id+"F4.wireOp",EDGE,"E10.sketch_text.stroke-72"),sQuery(id+"F4.wireOp",EDGE,"E10.sketch_text.stroke-73"),sQuery(id+"F4.wireOp",EDGE,"E10.sketch_text.stroke-74"),sQuery(id+"F4.wireOp",EDGE,"E10.sketch_text.stroke-75"),sQuery(id+"F4.wireOp",EDGE,"E10.sketch_text.stroke-76"),sQuery(id+"F4.wireOp",EDGE,"E10.sketch_text.stroke-77"),sQuery(id+"F4.wireOp",EDGE,"E10.sketch_text.stroke-78"),sQuery(id+"F4.wireOp",EDGE,"E10.sketch_text.stroke-79"),sQuery(id+"F4.wireOp",EDGE,"E10.sketch_text.stroke-80"),sQuery(id+"F4.wireOp",EDGE,"E10.sketch_text.stroke-81"),sQuery(id+"F4.wireOp",EDGE,"E10.sketch_text.stroke-82"),sQuery(id+"F4.wireOp",EDGE,"E10.sketch_text.stroke-83"),sQuery(id+"F4.wireOp",EDGE,"E10.sketch_text.stroke-84"),sQuery(id+"F4.wireOp",EDGE,"E10.sketch_text.stroke-85"),sQuery(id+"F4.wireOp",EDGE,"E10.sketch_text.stroke-86"),sQuery(id+"F4.wireOp",EDGE,"E10.sketch_text.stroke-87"),sQuery(id+"F4.wireOp",EDGE,"E10.sketch_text.stroke-88"),sQuery(id+"F4.wireOp",EDGE,"E10.sketch_text.stroke-89"),sQuery(id+"F4.wireOp",EDGE,"E10.sketch_text.stroke-90"),sQuery(id+"F4.wireOp",EDGE,"E10.sketch_text.stroke-91"),sQuery(id+"F4.wireOp",EDGE,"E10.sketch_text.stroke-92"),sQuery(id+"F4.wireOp",EDGE,"E10.sketch_text.stroke-93"),sQuery(id+"F4.wireOp",EDGE,"E10.sketch_text.stroke-94"),sQuery(id+"F4.wireOp",EDGE,"E10.sketch_text.stroke-95"),sQuery(id+"F4.wireOp",EDGE,"E10.sketch_text.stroke-96"),sQuery(id+"F4.wireOp",EDGE,"E10.sketch_text.stroke-97"),sQuery(id+"F4.wireOp",EDGE,"E10.sketch_text.stroke-98"),sQuery(id+"F4.wireOp",EDGE,"E10.sketch_text.stroke-99"),sQuery(id+"F4.wireOp",EDGE,"E10.sketch_text.stroke-100"),sQuery(id+"F4.wireOp",EDGE,"E10.sketch_text.stroke-101"),sQuery(id+"F4.wireOp",EDGE,"E10.sketch_text.stroke-102"),sQuery(id+"F4.wireOp",EDGE,"E10.sketch_text.stroke-103"),sQuery(id+"F4.wireOp",EDGE,"E10.sketch_text.stroke-104")])],"isStart":false});
            var Q117;
            Q117=makeQuery(id+"F5.opExtrude","SWEPT_FACE",FACE,{"disambiguationData":[OSD([sQuery(id+"F4.wireOp",EDGE,"E10.sketch_text.stroke-33")])]});
            var Q118;
            Q118=makeQuery(id+"F5.opExtrude","SWEPT_FACE",FACE,{"disambiguationData":[OSD([sQuery(id+"F4.wireOp",EDGE,"E10.sketch_text.stroke-93")])]});
            var Q119;
            Q119=makeQuery(id+"F5.opExtrude","SWEPT_FACE",FACE,{"disambiguationData":[OSD([sQuery(id+"F4.wireOp",EDGE,"E10.sketch_text.stroke-34")])]});
            var Q120;
            Q120=makeQuery(id+"F5.opExtrude","SWEPT_FACE",FACE,{"disambiguationData":[OSD([sQuery(id+"F4.wireOp",EDGE,"E10.sketch_text.stroke-152")])]});
            var Q121;
            Q121=makeQuery(id+"F5.opExtrude","SWEPT_FACE",FACE,{"disambiguationData":[OSD([sQuery(id+"F4.wireOp",EDGE,"E10.sketch_text.stroke-51")])]});
            var Q122;
            Q122=makeQuery(id+"F5.opExtrude","SWEPT_FACE",FACE,{"disambiguationData":[OSD([sQuery(id+"F4.wireOp",EDGE,"E10.sketch_text.stroke-6")])]});
            var Q123;
            Q123=makeQuery(id+"F5.opExtrude","SWEPT_FACE",FACE,{"disambiguationData":[OSD([sQuery(id+"F4.wireOp",EDGE,"E10.sketch_text.stroke-7")])]});
            var Q124;
            Q124=makeQuery(id+"F5.opExtrude","SWEPT_FACE",FACE,{"disambiguationData":[OSD([sQuery(id+"F4.wireOp",EDGE,"E10.sketch_text.stroke-156")])]});
            var Q125;
            Q125=makeQuery(id+"F5.opExtrude","SWEPT_FACE",FACE,{"disambiguationData":[OSD([sQuery(id+"F4.wireOp",EDGE,"E10.sketch_text.stroke-112")])]});
            var Q126;
            Q126=makeQuery(id+"F5.boolean.opBoolean","SPLIT",FACE,{"disambiguationData":[TD([makeQuery(id+"F5.opExtrude","SWEPT_FACE",FACE,{"disambiguationData":[OSD([sQuery(id+"F4.wireOp",EDGE,"E10.sketch_text.stroke-182")])]})])],"derivedFrom":makeQuery(id+"F1.opExtrude","CAP_FACE",FACE,{"disambiguationData":[OSD([sQuery(id+"F0.wireOp",EDGE,"E0.bottom"),sQuery(id+"F0.wireOp",EDGE,"E0.top"),sQuery(id+"F0.wireOp",EDGE,"E0.left"),sQuery(id+"F0.wireOp",EDGE,"E0.right"),sQuery(id+"F0.wireOp",EDGE,"E1"),sQuery(id+"F0.wireOp",EDGE,"E7.MirrorC"),sQuery(id+"F0.wireOp",EDGE,"E8.MirrorC"),sQuery(id+"F0.wireOp",EDGE,"E9.MirrorC")])],"isStart":true})});
            var Q127;
            Q127=makeQuery(id+"F5.opExtrude","SWEPT_FACE",FACE,{"disambiguationData":[OSD([sQuery(id+"F4.wireOp",EDGE,"E10.sketch_text.stroke-96")])]});
            var Q128;
            Q128=makeQuery(id+"F5.opExtrude","SWEPT_FACE",FACE,{"disambiguationData":[OSD([sQuery(id+"F4.wireOp",EDGE,"E10.sketch_text.stroke-114")])]});
            var Q129;
            Q129=makeQuery(id+"F5.opExtrude","SWEPT_FACE",FACE,{"disambiguationData":[OSD([sQuery(id+"F4.wireOp",EDGE,"E10.sketch_text.stroke-39")])]});
            var Q130;
            Q130=makeQuery(id+"F5.opExtrude","SWEPT_FACE",FACE,{"disambiguationData":[OSD([sQuery(id+"F4.wireOp",EDGE,"E10.sketch_text.stroke-13")])]});
            var Q131;
            Q131=makeQuery(id+"F5.opExtrude","SWEPT_FACE",FACE,{"disambiguationData":[OSD([sQuery(id+"F4.wireOp",EDGE,"E10.sketch_text.stroke-115")])]});
            var Q132;
            Q132=makeQuery(id+"F5.opExtrude","SWEPT_FACE",FACE,{"disambiguationData":[OSD([sQuery(id+"F4.wireOp",EDGE,"E10.sketch_text.stroke-56")])]});
            var Q133;
            Q133=makeQuery(id+"F5.opExtrude","SWEPT_FACE",FACE,{"disambiguationData":[OSD([sQuery(id+"F4.wireOp",EDGE,"E10.sketch_text.stroke-144")])]});
            var Q134;
            Q134=makeQuery(id+"F5.opExtrude","SWEPT_FACE",FACE,{"disambiguationData":[OSD([sQuery(id+"F4.wireOp",EDGE,"E10.sketch_text.stroke-190")])]});
            var Q135;
            Q135=makeQuery(id+"F5.opExtrude","SWEPT_FACE",FACE,{"disambiguationData":[OSD([sQuery(id+"F4.wireOp",EDGE,"E10.sketch_text.stroke-116")])]});
            var Q136;
            Q136=makeQuery(id+"F5.opExtrude","SWEPT_FACE",FACE,{"disambiguationData":[OSD([sQuery(id+"F4.wireOp",EDGE,"E10.sketch_text.stroke-41")])]});
            var Q137;
            Q137=makeQuery(id+"F5.opExtrude","SWEPT_FACE",FACE,{"disambiguationData":[OSD([sQuery(id+"F4.wireOp",EDGE,"E10.sketch_text.stroke-161")])]});
            var Q138;
            Q138=makeQuery(id+"F5.opExtrude","SWEPT_FACE",FACE,{"disambiguationData":[OSD([sQuery(id+"F4.wireOp",EDGE,"E10.sketch_text.stroke-146")])]});
            var Q139;
            Q139=makeQuery(id+"F5.opExtrude","SWEPT_FACE",FACE,{"disambiguationData":[OSD([sQuery(id+"F4.wireOp",EDGE,"E10.sketch_text.stroke-58")])]});
            var Q140;
            Q140=makeQuery(id+"F5.opExtrude","SWEPT_FACE",FACE,{"disambiguationData":[OSD([sQuery(id+"F4.wireOp",EDGE,"E10.sketch_text.stroke-105")])]});
            var Q141;
            Q141=makeQuery(id+"F5.opExtrude","SWEPT_FACE",FACE,{"disambiguationData":[OSD([sQuery(id+"F4.wireOp",EDGE,"E10.sketch_text.stroke-177")])]});
            var Q142;
            Q142=makeQuery(id+"F5.opExtrude","SWEPT_FACE",FACE,{"disambiguationData":[OSD([sQuery(id+"F4.wireOp",EDGE,"E10.sketch_text.stroke-77")])]});
            var Q143;
            Q143=makeQuery(id+"F5.opExtrude","SWEPT_FACE",FACE,{"disambiguationData":[OSD([sQuery(id+"F4.wireOp",EDGE,"E10.sketch_text.stroke-138")])]});
            var Q144;
            Q144=makeQuery(id+"F5.opExtrude","SWEPT_FACE",FACE,{"disambiguationData":[OSD([sQuery(id+"F4.wireOp",EDGE,"E10.sketch_text.stroke-111")])]});
            var Q145;
            Q145=makeQuery(id+"F5.opExtrude","SWEPT_FACE",FACE,{"disambiguationData":[OSD([sQuery(id+"F4.wireOp",EDGE,"E10.sketch_text.stroke-53")])]});
            var Q146;
            Q146=makeQuery(id+"F5.opExtrude","SWEPT_FACE",FACE,{"disambiguationData":[OSD([sQuery(id+"F4.wireOp",EDGE,"E10.sketch_text.stroke-141")])]});
            var Q147;
            Q147=makeQuery(id+"F5.opExtrude","SWEPT_FACE",FACE,{"disambiguationData":[OSD([sQuery(id+"F4.wireOp",EDGE,"E10.sketch_text.stroke-157")])]});
            var Q148;
            Q148=makeQuery(id+"F5.opExtrude","SWEPT_FACE",FACE,{"disambiguationData":[OSD([sQuery(id+"F4.wireOp",EDGE,"E10.sketch_text.stroke-64")])]});
            var Q149;
            Q149=makeQuery(id+"F5.boolean.opBoolean","SPLIT",FACE,{"disambiguationData":[TD([makeQuery(id+"F5.opExtrude","SWEPT_FACE",FACE,{"disambiguationData":[OSD([sQuery(id+"F4.wireOp",EDGE,"E10.sketch_text.stroke-53")])]})])],"derivedFrom":makeQuery(id+"F1.opExtrude","CAP_FACE",FACE,{"disambiguationData":[OSD([sQuery(id+"F0.wireOp",EDGE,"E0.bottom"),sQuery(id+"F0.wireOp",EDGE,"E0.top"),sQuery(id+"F0.wireOp",EDGE,"E0.left"),sQuery(id+"F0.wireOp",EDGE,"E0.right"),sQuery(id+"F0.wireOp",EDGE,"E1"),sQuery(id+"F0.wireOp",EDGE,"E7.MirrorC"),sQuery(id+"F0.wireOp",EDGE,"E8.MirrorC"),sQuery(id+"F0.wireOp",EDGE,"E9.MirrorC")])],"isStart":true})});
            var Q150;
            Q150=makeQuery(id+"F5.opExtrude","SWEPT_FACE",FACE,{"disambiguationData":[OSD([sQuery(id+"F4.wireOp",EDGE,"E10.sketch_text.stroke-36")])]});
            var Q151;
            Q151=makeQuery(id+"F5.opExtrude","SWEPT_FACE",FACE,{"disambiguationData":[OSD([sQuery(id+"F4.wireOp",EDGE,"E10.sketch_text.stroke-22")])]});
            var Q152;
            Q152=makeQuery(id+"F5.boolean.opBoolean","SPLIT",FACE,{"disambiguationData":[TD([makeQuery(id+"F5.opExtrude","SWEPT_FACE",FACE,{"disambiguationData":[OSD([sQuery(id+"F4.wireOp",EDGE,"E10.sketch_text.stroke-119")])]})])],"derivedFrom":makeQuery(id+"F1.opExtrude","CAP_FACE",FACE,{"disambiguationData":[OSD([sQuery(id+"F0.wireOp",EDGE,"E0.bottom"),sQuery(id+"F0.wireOp",EDGE,"E0.top"),sQuery(id+"F0.wireOp",EDGE,"E0.left"),sQuery(id+"F0.wireOp",EDGE,"E0.right"),sQuery(id+"F0.wireOp",EDGE,"E1"),sQuery(id+"F0.wireOp",EDGE,"E7.MirrorC"),sQuery(id+"F0.wireOp",EDGE,"E8.MirrorC"),sQuery(id+"F0.wireOp",EDGE,"E9.MirrorC")])],"isStart":true})});
            var Q153;
            Q153=makeQuery(id+"F5.boolean.opBoolean","SPLIT",FACE,{"disambiguationData":[TD([makeQuery(id+"F5.opExtrude","SWEPT_FACE",FACE,{"disambiguationData":[OSD([sQuery(id+"F4.wireOp",EDGE,"E10.sketch_text.stroke-158")])]})])],"derivedFrom":makeQuery(id+"F1.opExtrude","CAP_FACE",FACE,{"disambiguationData":[OSD([sQuery(id+"F0.wireOp",EDGE,"E0.bottom"),sQuery(id+"F0.wireOp",EDGE,"E0.top"),sQuery(id+"F0.wireOp",EDGE,"E0.left"),sQuery(id+"F0.wireOp",EDGE,"E0.right"),sQuery(id+"F0.wireOp",EDGE,"E1"),sQuery(id+"F0.wireOp",EDGE,"E7.MirrorC"),sQuery(id+"F0.wireOp",EDGE,"E8.MirrorC"),sQuery(id+"F0.wireOp",EDGE,"E9.MirrorC")])],"isStart":true})});
            var Q154;
            Q154=makeQuery(id+"F5.opExtrude","SWEPT_FACE",FACE,{"disambiguationData":[OSD([sQuery(id+"F4.wireOp",EDGE,"E10.sketch_text.stroke-9")])]});
            var Q155;
            Q155=makeQuery(id+"F5.opExtrude","SWEPT_FACE",FACE,{"disambiguationData":[OSD([sQuery(id+"F4.wireOp",EDGE,"E10.sketch_text.stroke-167")])]});
            var Q156;
            Q156=makeQuery(id+"F5.opExtrude","SWEPT_FACE",FACE,{"disambiguationData":[OSD([sQuery(id+"F4.wireOp",EDGE,"E10.sketch_text.stroke-95")])]});
            var Q157;
            Q157=makeQuery(id+"F5.opExtrude","SWEPT_FACE",FACE,{"disambiguationData":[OSD([sQuery(id+"F4.wireOp",EDGE,"E10.sketch_text.stroke-184")])]});
            var Q158;
            Q158=makeQuery(id+"F5.opExtrude","SWEPT_FACE",FACE,{"disambiguationData":[OSD([sQuery(id+"F4.wireOp",EDGE,"E10.sketch_text.stroke-84")])]});
            var Q159;
            Q159=makeQuery(id+"F5.opExtrude","SWEPT_FACE",FACE,{"disambiguationData":[OSD([sQuery(id+"F4.wireOp",EDGE,"E10.sketch_text.stroke-68")])]});
            var Q160;
            Q160=makeQuery(id+"F5.opExtrude","SWEPT_FACE",FACE,{"disambiguationData":[OSD([sQuery(id+"F4.wireOp",EDGE,"E10.sketch_text.stroke-143")])]});
            var Q161;
            Q161=makeQuery(id+"F5.opExtrude","SWEPT_FACE",FACE,{"disambiguationData":[OSD([sQuery(id+"F4.wireOp",EDGE,"E10.sketch_text.stroke-189")])]});
            var Q162;
            Q162=makeQuery(id+"F5.opExtrude","CAP_FACE",FACE,{"disambiguationData":[OSD([sQuery(id+"F4.wireOp",EDGE,"E10.sketch_text.stroke-13"),sQuery(id+"F4.wireOp",EDGE,"E10.sketch_text.stroke-14"),sQuery(id+"F4.wireOp",EDGE,"E10.sketch_text.stroke-15"),sQuery(id+"F4.wireOp",EDGE,"E10.sketch_text.stroke-16"),sQuery(id+"F4.wireOp",EDGE,"E10.sketch_text.stroke-17"),sQuery(id+"F4.wireOp",EDGE,"E10.sketch_text.stroke-18"),sQuery(id+"F4.wireOp",EDGE,"E10.sketch_text.stroke-19"),sQuery(id+"F4.wireOp",EDGE,"E10.sketch_text.stroke-20")])],"isStart":false});
            var Q163;
            Q163=makeQuery(id+"F5.opExtrude","SWEPT_FACE",FACE,{"disambiguationData":[OSD([sQuery(id+"F4.wireOp",EDGE,"E10.sketch_text.stroke-57")])]});
            var Q164;
            Q164=makeQuery(id+"F5.opExtrude","SWEPT_FACE",FACE,{"disambiguationData":[OSD([sQuery(id+"F4.wireOp",EDGE,"E10.sketch_text.stroke-29")])]});
            var Q165;
            Q165=makeQuery(id+"F5.opExtrude","SWEPT_FACE",FACE,{"disambiguationData":[OSD([sQuery(id+"F4.wireOp",EDGE,"E10.sketch_text.stroke-60")])]});
            var Q166;
            Q166=makeQuery(id+"F5.opExtrude","SWEPT_FACE",FACE,{"disambiguationData":[OSD([sQuery(id+"F4.wireOp",EDGE,"E10.sketch_text.stroke-148")])]});
            var Q167;
            Q167=makeQuery(id+"F5.opExtrude","SWEPT_FACE",FACE,{"disambiguationData":[OSD([sQuery(id+"F4.wireOp",EDGE,"E10.sketch_text.stroke-75")])]});
            var Q168;
            Q168=makeQuery(id+"F5.opExtrude","SWEPT_FACE",FACE,{"disambiguationData":[OSD([sQuery(id+"F4.wireOp",EDGE,"E10.sketch_text.stroke-91")])]});
            var Q169;
            Q169=makeQuery(id+"F5.opExtrude","SWEPT_FACE",FACE,{"disambiguationData":[OSD([sQuery(id+"F4.wireOp",EDGE,"E10.sketch_text.stroke-78")])]});
            var Q170;
            Q170=makeQuery(id+"F5.opExtrude","SWEPT_FACE",FACE,{"disambiguationData":[OSD([sQuery(id+"F4.wireOp",EDGE,"E10.sketch_text.stroke-62")])]});
            var Q171;
            Q171=makeQuery(id+"F5.opExtrude","SWEPT_FACE",FACE,{"disambiguationData":[OSD([sQuery(id+"F4.wireOp",EDGE,"E10.sketch_text.stroke-182")])]});
            var Q172;
            Q172=makeQuery(id+"F5.opExtrude","SWEPT_FACE",FACE,{"disambiguationData":[OSD([sQuery(id+"F4.wireOp",EDGE,"E10.sketch_text.stroke-11")])]});
            var Q173;
            Q173=makeQuery(id+"F5.opExtrude","SWEPT_FACE",FACE,{"disambiguationData":[OSD([sQuery(id+"F4.wireOp",EDGE,"E10.sketch_text.stroke-97")])]});
            var Q174;
            Q174=makeQuery(id+"F5.opExtrude","SWEPT_FACE",FACE,{"disambiguationData":[OSD([sQuery(id+"F4.wireOp",EDGE,"E10.sketch_text.stroke-23")])]});
            var Q175;
            Q175=makeQuery(id+"F5.opExtrude","SWEPT_FACE",FACE,{"disambiguationData":[OSD([sQuery(id+"F4.wireOp",EDGE,"E10.sketch_text.stroke-80")])]});
            var Q176;
            Q176=makeQuery(id+"F5.boolean.opBoolean","SPLIT",FACE,{"disambiguationData":[TD([makeQuery(id+"F5.opExtrude","SWEPT_FACE",FACE,{"disambiguationData":[OSD([sQuery(id+"F4.wireOp",EDGE,"E10.sketch_text.stroke-99")])]})])],"derivedFrom":makeQuery(id+"F1.opExtrude","CAP_FACE",FACE,{"disambiguationData":[OSD([sQuery(id+"F0.wireOp",EDGE,"E0.bottom"),sQuery(id+"F0.wireOp",EDGE,"E0.top"),sQuery(id+"F0.wireOp",EDGE,"E0.left"),sQuery(id+"F0.wireOp",EDGE,"E0.right"),sQuery(id+"F0.wireOp",EDGE,"E1"),sQuery(id+"F0.wireOp",EDGE,"E7.MirrorC"),sQuery(id+"F0.wireOp",EDGE,"E8.MirrorC"),sQuery(id+"F0.wireOp",EDGE,"E9.MirrorC")])],"isStart":true})});
            var Q177;
            Q177=makeQuery(id+"F5.opExtrude","SWEPT_FACE",FACE,{"disambiguationData":[OSD([sQuery(id+"F4.wireOp",EDGE,"E10.sketch_text.stroke-168")])]});
            var Q178;
            Q178=makeQuery(id+"F5.opExtrude","SWEPT_FACE",FACE,{"disambiguationData":[OSD([sQuery(id+"F4.wireOp",EDGE,"E10.sketch_text.stroke-188")])]});
            var Q179;
            Q179=makeQuery(id+"F5.opExtrude","SWEPT_FACE",FACE,{"disambiguationData":[OSD([sQuery(id+"F4.wireOp",EDGE,"E10.sketch_text.stroke-129")])]});
            var Q180;
            Q180=makeQuery(id+"F5.opExtrude","SWEPT_FACE",FACE,{"disambiguationData":[OSD([sQuery(id+"F4.wireOp",EDGE,"E10.sketch_text.stroke-27")])]});
            var Q181;
            Q181=makeQuery(id+"F5.opExtrude","SWEPT_FACE",FACE,{"disambiguationData":[OSD([sQuery(id+"F4.wireOp",EDGE,"E10.sketch_text.stroke-175")])]});
            var Q182;
            Q182=makeQuery(id+"F5.opExtrude","SWEPT_FACE",FACE,{"disambiguationData":[OSD([sQuery(id+"F4.wireOp",EDGE,"E10.sketch_text.stroke-42")])]});
            var Q183;
            Q183=makeQuery(id+"F5.opExtrude","SWEPT_FACE",FACE,{"disambiguationData":[OSD([sQuery(id+"F4.wireOp",EDGE,"E10.sketch_text.stroke-118")])]});
            var Q184;
            Q184=makeQuery(id+"F5.opExtrude","SWEPT_FACE",FACE,{"disambiguationData":[OSD([sQuery(id+"F4.wireOp",EDGE,"E10.sketch_text.stroke-151")])]});
            var Q185;
            Q185=makeQuery(id+"F5.opExtrude","SWEPT_FACE",FACE,{"disambiguationData":[OSD([sQuery(id+"F4.wireOp",EDGE,"E10.sketch_text.stroke-137")])]});
            var Q186;
            Q186=makeQuery(id+"F5.opExtrude","SWEPT_FACE",FACE,{"disambiguationData":[OSD([sQuery(id+"F4.wireOp",EDGE,"E10.sketch_text.stroke-83")])]});
            var Q187;
            Q187=makeQuery(id+"F5.boolean.opBoolean","SPLIT",FACE,{"disambiguationData":[TD([makeQuery(id+"F5.opExtrude","SWEPT_FACE",FACE,{"disambiguationData":[OSD([sQuery(id+"F4.wireOp",EDGE,"E10.sketch_text.stroke-90")])]})])],"derivedFrom":makeQuery(id+"F1.opExtrude","CAP_FACE",FACE,{"disambiguationData":[OSD([sQuery(id+"F0.wireOp",EDGE,"E0.bottom"),sQuery(id+"F0.wireOp",EDGE,"E0.top"),sQuery(id+"F0.wireOp",EDGE,"E0.left"),sQuery(id+"F0.wireOp",EDGE,"E0.right"),sQuery(id+"F0.wireOp",EDGE,"E1"),sQuery(id+"F0.wireOp",EDGE,"E7.MirrorC"),sQuery(id+"F0.wireOp",EDGE,"E8.MirrorC"),sQuery(id+"F0.wireOp",EDGE,"E9.MirrorC")])],"isStart":true})});
            var Q188;
            Q188=makeQuery(id+"F5.opExtrude","SWEPT_FACE",FACE,{"disambiguationData":[OSD([sQuery(id+"F4.wireOp",EDGE,"E10.sketch_text.stroke-139")])]});
            var Q189;
            Q189=makeQuery(id+"F5.opExtrude","SWEPT_FACE",FACE,{"disambiguationData":[OSD([sQuery(id+"F4.wireOp",EDGE,"E10.sketch_text.stroke-70")])]});
            var Q190;
            Q190=makeQuery(id+"F5.opExtrude","SWEPT_FACE",FACE,{"disambiguationData":[OSD([sQuery(id+"F4.wireOp",EDGE,"E10.sketch_text.stroke-160")])]});
            var Q191;
            Q191=makeQuery(id+"F5.opExtrude","SWEPT_FACE",FACE,{"disambiguationData":[OSD([sQuery(id+"F4.wireOp",EDGE,"E10.sketch_text.stroke-71")])]});
            var Q192;
            Q192=makeQuery(id+"F5.opExtrude","SWEPT_FACE",FACE,{"disambiguationData":[OSD([sQuery(id+"F4.wireOp",EDGE,"E10.sketch_text.stroke-117")])]});
            var Q193;
            Q193=makeQuery(id+"F5.opExtrude","SWEPT_FACE",FACE,{"disambiguationData":[OSD([sQuery(id+"F4.wireOp",EDGE,"E10.sketch_text.stroke-147")])]});
            var Q194;
            Q194=makeQuery(id+"F5.opExtrude","SWEPT_FACE",FACE,{"disambiguationData":[OSD([sQuery(id+"F4.wireOp",EDGE,"E10.sketch_text.stroke-164")])]});
            var Q195;
            Q195=makeQuery(id+"F5.opExtrude","SWEPT_FACE",FACE,{"disambiguationData":[OSD([sQuery(id+"F4.wireOp",EDGE,"E10.sketch_text.stroke-61")])]});
            var Q196;
            Q196=makeQuery(id+"F5.opExtrude","SWEPT_FACE",FACE,{"disambiguationData":[OSD([sQuery(id+"F4.wireOp",EDGE,"E10.sketch_text.stroke-19")])]});
            var Q197;
            Q197=makeQuery(id+"F5.opExtrude","SWEPT_FACE",FACE,{"disambiguationData":[OSD([sQuery(id+"F4.wireOp",EDGE,"E10.sketch_text.stroke-35")])]});
            var Q198;
            Q198=makeQuery(id+"F5.opExtrude","SWEPT_FACE",FACE,{"disambiguationData":[OSD([sQuery(id+"F4.wireOp",EDGE,"E10.sketch_text.stroke-140")])]});
            var Q199;
            Q199=makeQuery(id+"F5.opExtrude","SWEPT_FACE",FACE,{"disambiguationData":[OSD([sQuery(id+"F4.wireOp",EDGE,"E10.sketch_text.stroke-20")])]});
            var Q200;
            Q200=makeQuery(id+"F5.opExtrude","SWEPT_FACE",FACE,{"disambiguationData":[OSD([sQuery(id+"F4.wireOp",EDGE,"E10.sketch_text.stroke-16")])]});
            var Q201;
            Q201=makeQuery(id+"F5.opExtrude","SWEPT_FACE",FACE,{"disambiguationData":[OSD([sQuery(id+"F4.wireOp",EDGE,"E10.sketch_text.stroke-18")])]});
            var Q202;
            Q202=makeQuery(id+"F5.opExtrude","SWEPT_FACE",FACE,{"disambiguationData":[OSD([sQuery(id+"F4.wireOp",EDGE,"E10.sketch_text.stroke-17")])]});
            var Q203;
            Q203=qCreatedBy(makeId("Right.planeOp"),FACE);
            mirror(context, id + "F6", {"operationType" : NewBodyOperationType.ADD, "entities" : qUnion([Q0]), "faces" : qUnion([Q1, Q2, Q3, Q4, Q5, Q6, Q7, Q8, Q9, Q10, Q11, Q12, Q13, Q14, Q15, Q16, Q17, Q18, Q19, Q20, Q21, Q22, Q23, Q24, Q25, Q26, Q27, Q28, Q29, Q30, Q31, Q32, Q33, Q34, Q35, Q36, Q37, Q38, Q39, Q40, Q41, Q42, Q43, Q44, Q45, Q46, Q47, Q48, Q49, Q50, Q51, Q52, Q53, Q54, Q55, Q56, Q57, Q58, Q59, Q60, Q61, Q62, Q63, Q64, Q65, Q66, Q67, Q68, Q69, Q70, Q71, Q72, Q73, Q74, Q75, Q76, Q77, Q78, Q79, Q80, Q81, Q82, Q83, Q84, Q85, Q86, Q87, Q88, Q89, Q90, Q91, Q92, Q93, Q94, Q95, Q96, Q97, Q98, Q99, Q100, Q101, Q102, Q103, Q104, Q105, Q106, Q107, Q108, Q109, Q110, Q111, Q112, Q113, Q114, Q115, Q116, Q117, Q118, Q119, Q120, Q121, Q122, Q123, Q124, Q125, Q126, Q127, Q128, Q129, Q130, Q131, Q132, Q133, Q134, Q135, Q136, Q137, Q138, Q139, Q140, Q141, Q142, Q143, Q144, Q145, Q146, Q147, Q148, Q149, Q150, Q151, Q152, Q153, Q154, Q155, Q156, Q157, Q158, Q159, Q160, Q161, Q162, Q163, Q164, Q165, Q166, Q167, Q168, Q169, Q170, Q171, Q172, Q173, Q174, Q175, Q176, Q177, Q178, Q179, Q180, Q181, Q182, Q183, Q184, Q185, Q186, Q187, Q188, Q189, Q190, Q191, Q192, Q193, Q194, Q195, Q196, Q197, Q198, Q199, Q200, Q201, Q202]), "mirrorPlane" : qUnion([Q203])});
        }
    });
